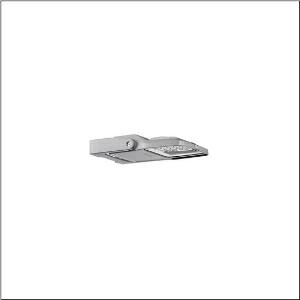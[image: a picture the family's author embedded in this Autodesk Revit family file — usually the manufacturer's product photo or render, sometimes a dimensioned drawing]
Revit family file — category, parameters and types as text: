
# Revit family: floodlight_fl_21_iq_micro___pl33t_5xa7762a4f2a_0497
name_source: partatom
category: Lighting Fixtures
units: mm (PartAtom-declared; Revit-internal decimal feet)

## family parameters
Cut with Voids When Loaded = No
Host = Face
Light Source = No
Part Type = Normal
Room Calculation Point = No
Round Connector Dimension = Use Diameter
Shared = No

## types (1)
- --- (1 x LED, 3050 lm, 23.1 W, 4000K)
    Apparent Load = 23 VA
    CIE Flux Codes = 26 75 99 100 100
    Color Rendering = 70
    Color Temperature = 4000K
    Default Elevation = 1800 mm
    Description = Floodlight FL 21 iQ micro, floodlight, primary light control with lens, of PMMA, primary optical cover: protective disc, of toughened safety glass, transparent, light distribution: PL33T, light emission: direct distribution, installation type: surface-mounted, lamps: LED, High Power LED, rated values: 3.050lm | 23,1W | 132lm/W (begin service life); end service life: 3.050lm | 23,8W; at 50% lumin. flux: 1.525lm | 11W | 138,6lm/W, colour temperature: 4000K, colour rendering: CRI > 70, light colour: 740, light setting 1 begin service life: 100% | 3.050lm | 23,1W | 132lm/W | 4.000K, light setting 1 end service life: 23,8W, further light settings possible, control: Auto-Match, Temp-Guard, Night-Set, Smart-Wire, Desk-Remote (wireless, voltage-free reading and setting of iQ features in the workshop via application-optimized NFC function/RFID function), optimised constant luminous flux control (CLO 2.0), Street-Remote, pre-setting: linear dimming characteristic, with terminal, 6-pole, mains connection: 220..240V, AC, 50/60Hz, luminaire housing, of diecast aluminium, powder-coated, SITECO metallic grey (DB 702S), corrosivity category C5 mid according to DIN EN ISO 12944suitable for swimming poolschlorine-resistant, sealing non-destructively replaceable, design bracket, of diecast aluminium, powder-coated, SITECO metallic grey (DB 702S), protection rating (complete): IP66, insulation class (complete): insulation class II (safety insulation), certification: CE, ENEC, VDE, protection symbol: D, impact resistance: IK07, permissible operating ambient temperature: -40..+40°C, permissible operating ambient temperature for outdoor applications: -40..+50°C, standard: DIN EN 12944, LABS conformity tested according to VDMA 24364:2018-05, packaging unit: 1 piece

Light Distribution: PL33T
    Height = 65 mm
    Lamp = 1 x LED
    Lamp Light Flux = 3050 lm
    Lamp Power = 23.1 W
    Lamp count = 1
    Length = 312 mm
    Luminous efficacy = 132 lm/W
    Manufacturer = Siteco
    ModVariant = No
    Model = 5XA7762A4F2A
    Mounting Place = Wall
    Mounting Type = Surface mounted
    Number of Poles = 1
    OnlyDefault = Yes
    Power Factor = 1
    Product Name = Floodlight FL 21 iQ micro | PL33T
    Product group = floodlight | wall mounted
    ProductGroupID = 2002
    Protection Class = Protection class II
    Protection Degree = IP 66
    RLX_Detail_Level = 1
    RLX_Emergency_Light_Flux = 0 lm
    RLX_Emergency_Type = 0
    RLX_Emergency_Type_DB = No
    RlxData = <blob elided: 97589 chars, md5=a38c020f>
    Socket = socket
    Standby Power = 0 W
    System Light Flux = 3050 lm
    System Power = 23 W
    Type Comments = factory setting: luminous flux: 100 % | dim-lin: 254 | 455 mA
    Type Image = l_1006878.jpg
    URL = http://relux.com
    VarID = @adj_148945
    Voltage = 0 V
    Weight = 0.00 kg
    Width = 230 mm

## geometry (parser evidence)
native form markers: Blend x4, Sweep x11
no freeform markers — native parametric forms only
